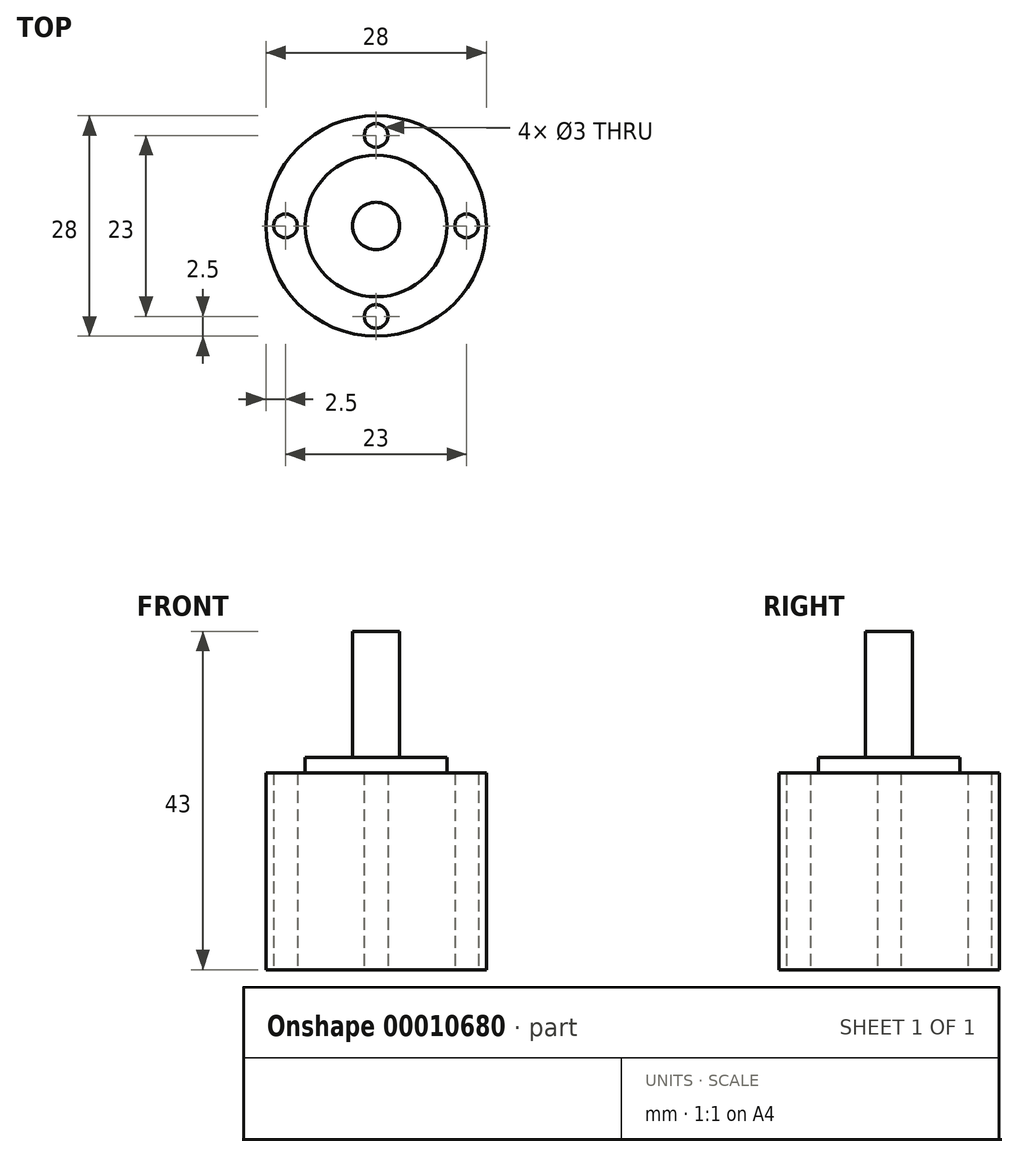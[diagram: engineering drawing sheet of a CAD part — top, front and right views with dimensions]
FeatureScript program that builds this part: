
annotation { "Feature Type Name" : "Feature", "Feature Type Description" : "" }
export const myFeature = defineFeature(function(context is Context, id is Id, definition is map)
    precondition{}
    {
        {
            var Q0;
            Q0=qCreatedBy(makeId("Top.planeOp"),FACE);
            var sketch = newSketch(context, id + "F0", { "sketchPlane" : qUnion([Q0])});
            skCircle(sketch, "E0", {"center": v(0, 0) * mm, "radius": 14 * mm});
            skCircle(sketch, "E1", {"center": v(-11.5, 0) * mm, "radius": 1.5 * mm});
            skCircle(sketch, "E2.1.0", {"center": v(0, -11.5) * mm, "radius": 1.5 * mm});
            skCircle(sketch, "E2.2.0", {"center": v(11.5, 0) * mm, "radius": 1.5 * mm});
            skCircle(sketch, "E2.3.0", {"center": v(0, 11.5) * mm, "radius": 1.5 * mm});
            skLineSegment(sketch, "E3", {"start": v(0, 11.5) * mm, "end": v(-11.5, 0) * mm, "construction": true});
            skLineSegment(sketch, "E4.0", {"start": v(-4.24, 15.74) * mm, "end": v(-15.74, 4.24) * mm});
            skSolve(sketch);
        }
        {
            var Q0;
            Q0=makeQuery(id+"F0.imprint","IMPRINT",FACE,{"disambiguationData":[TD([[makeQuery(id+"F0.imprint","IMPRINT",EDGE,{"derivedFrom":sQuery(id+"F0.wireOp",EDGE,"E0")}),1.0]])]});
            extrude(context, id + "F1", {"entities" : qUnion([Q0]), "depth" : 25 * mm});
        }
        {
            var Q0;
            Q0=makeQuery(id+"F1.opExtrude","CAP_FACE",FACE,{"disambiguationData":[OSD([sQuery(id+"F0.wireOp",EDGE,"E0"),sQuery(id+"F0.wireOp",EDGE,"E1"),sQuery(id+"F0.wireOp",EDGE,"E2.1.0"),sQuery(id+"F0.wireOp",EDGE,"E2.2.0"),sQuery(id+"F0.wireOp",EDGE,"E2.3.0")])],"isStart":false});
            var sketch = newSketch(context, id + "F2", { "sketchPlane" : qUnion([Q0])});
            skCircle(sketch, "E5", {"center": v(0, 0) * mm, "radius": 9 * mm});
            skSolve(sketch);
        }
        {
            var Q0;
            Q0 = qSketchRegion(id + "F2", true);
            extrude(context, id + "F3", {"entities" : qUnion([Q0]), "operationType" : NewBodyOperationType.ADD, "depth" : 2 * mm});
        }
        {
            var Q0;
            Q0=makeQuery(id+"F3.opExtrude","CAP_FACE",FACE,{"disambiguationData":[OSD([sQuery(id+"F2.wireOp",EDGE,"E5")])],"isStart":false});
            var sketch = newSketch(context, id + "F4", { "sketchPlane" : qUnion([Q0])});
            skCircle(sketch, "E6", {"center": v(0, 0) * mm, "radius": 3 * mm});
            skSolve(sketch);
        }
        {
            var Q0;
            Q0 = qSketchRegion(id + "F4", true);
            extrude(context, id + "F5", {"entities" : qUnion([Q0]), "operationType" : NewBodyOperationType.ADD, "depth" : 16 * mm});
        }
    });
